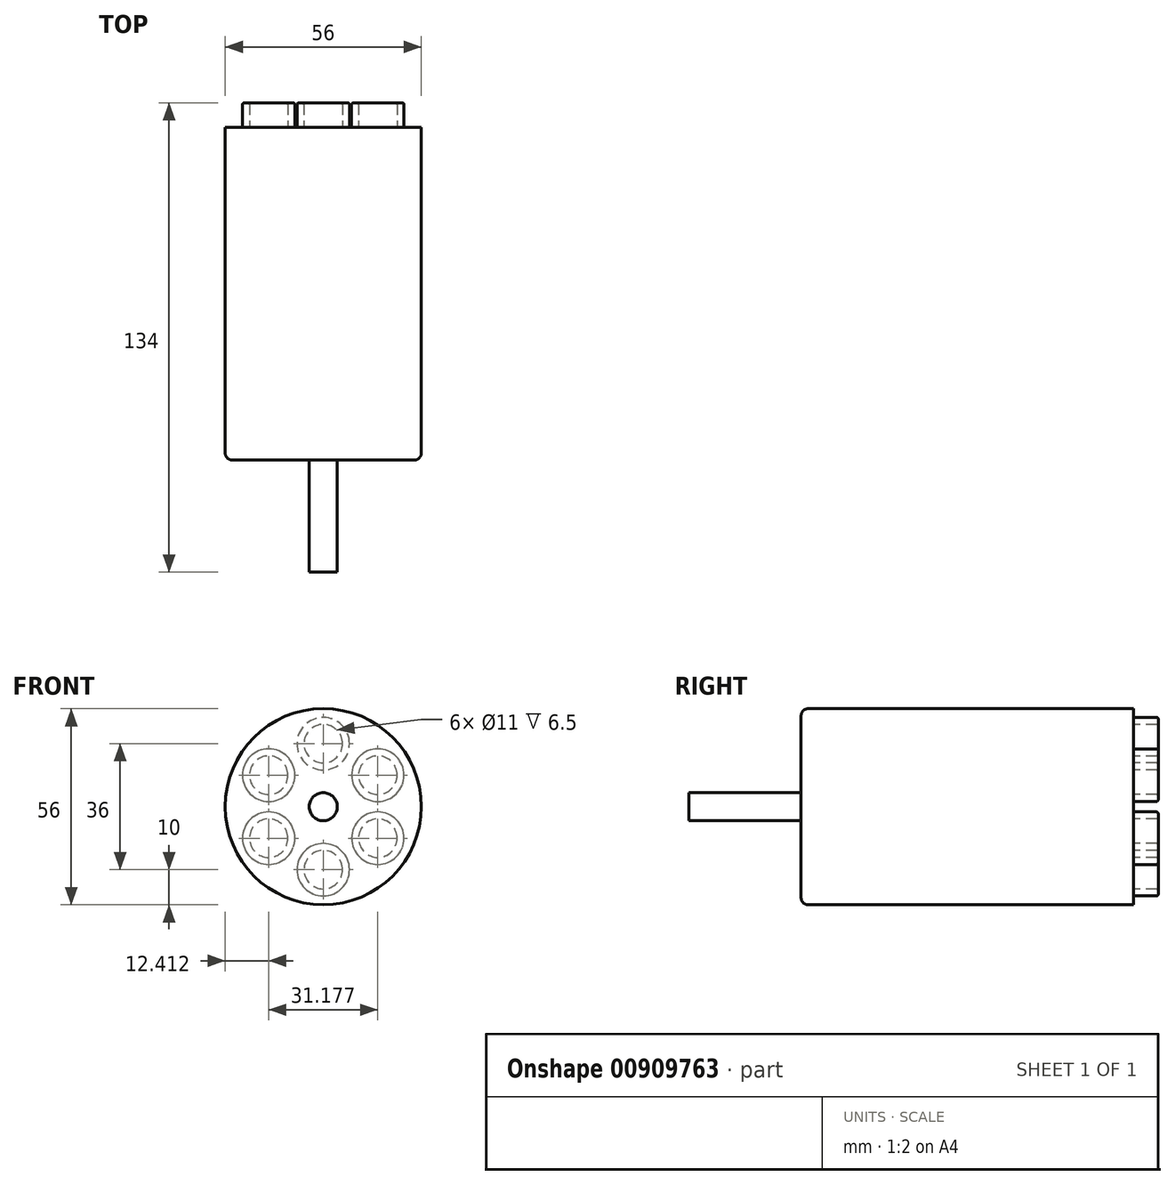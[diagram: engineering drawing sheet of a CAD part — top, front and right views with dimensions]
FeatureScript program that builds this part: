
annotation { "Feature Type Name" : "Feature", "Feature Type Description" : "" }
export const myFeature = defineFeature(function(context is Context, id is Id, definition is map)
    precondition{}
    {
        {
            var Q0;
            Q0=qCreatedBy(makeId("Front.planeOp"),FACE);
            var sketch = newSketch(context, id + "F0", { "sketchPlane" : qUnion([Q0])});
            skCircle(sketch, "E0", {"center": v(0, 0) * mm, "radius": 28 * mm});
            skSolve(sketch);
        }
        {
            var Q0;
            Q0 = qSketchRegion(id + "F0", true);
            extrude(context, id + "F1", {"entities" : qUnion([Q0]), "depth" : 95 * mm, "offsetDistance" : 25 * mm});
        }
        {
            var Q0;
            Q0=makeQuery(id+"F1.opExtrude","CAP_FACE",FACE,{"disambiguationData":[OSD([sQuery(id+"F0.wireOp",EDGE,"E0")])],"isStart":false});
            var sketch = newSketch(context, id + "F2", { "sketchPlane" : qUnion([Q0])});
            skCircle(sketch, "E1", {"center": v(0, 0) * mm, "radius": 4 * mm});
            skSolve(sketch);
        }
        {
            var Q0;
            Q0 = qSketchRegion(id + "F2", true);
            extrude(context, id + "F3", {"entities" : qUnion([Q0]), "operationType" : NewBodyOperationType.ADD, "depth" : 32 * mm, "offsetDistance" : 25 * mm});
        }
        {
            var Q0;
            Q0=makeQuery(id+"F1.opExtrude","CAP_FACE",FACE,{"disambiguationData":[OSD([sQuery(id+"F0.wireOp",EDGE,"E0")])],"isStart":true});
            var sketch = newSketch(context, id + "F4", { "sketchPlane" : qUnion([Q0])});
            skLineSegment(sketch, "E2", {"start": v(0, 0) * mm, "end": v(0, 18) * mm});
            skCircle(sketch, "E3", {"center": v(0, 18) * mm, "radius": 7.5 * mm});
            skCircle(sketch, "E4.1.0", {"center": v(-15.59, 9) * mm, "radius": 7.5 * mm});
            skLineSegment(sketch, "E4.1.1", {"start": v(0, 0) * mm, "end": v(-15.59, 9) * mm});
            skCircle(sketch, "E4.2.0", {"center": v(-15.59, -9) * mm, "radius": 7.5 * mm});
            skLineSegment(sketch, "E4.2.1", {"start": v(0, 0) * mm, "end": v(-15.59, -9) * mm});
            skCircle(sketch, "E4.3.0", {"center": v(0, -18) * mm, "radius": 7.5 * mm});
            skLineSegment(sketch, "E4.3.1", {"start": v(0, 0) * mm, "end": v(0, -18) * mm});
            skCircle(sketch, "E4.4.0", {"center": v(15.59, -9) * mm, "radius": 7.5 * mm});
            skLineSegment(sketch, "E4.4.1", {"start": v(0, 0) * mm, "end": v(15.59, -9) * mm});
            skCircle(sketch, "E4.5.0", {"center": v(15.59, 9) * mm, "radius": 7.5 * mm});
            skLineSegment(sketch, "E4.5.1", {"start": v(0, 0) * mm, "end": v(15.59, 9) * mm});
            skPoint(sketch, "E4.center", {"position": v(0, 0) * mm});
            skCircle(sketch, "E5", {"center": v(0, 18) * mm, "radius": 5.5 * mm});
            skCircle(sketch, "E6.1.0", {"center": v(-15.59, 9) * mm, "radius": 5.5 * mm});
            skCircle(sketch, "E6.2.0", {"center": v(-15.59, -9) * mm, "radius": 5.5 * mm});
            skCircle(sketch, "E6.3.0", {"center": v(0, -18) * mm, "radius": 5.5 * mm});
            skCircle(sketch, "E6.4.0", {"center": v(15.59, -9) * mm, "radius": 5.5 * mm});
            skCircle(sketch, "E6.5.0", {"center": v(15.59, 9) * mm, "radius": 5.5 * mm});
            skSolve(sketch);
        }
        {
            var Q0;
            Q0 = qSketchRegion(id + "F4", true);
            extrude(context, id + "F5", {"entities" : qUnion([Q0]), "operationType" : NewBodyOperationType.ADD, "depth" : 7 * mm, "offsetDistance" : 25 * mm});
        }
        {
            var Q0;
            Q0=makeQuery(id+"F5.opExtrude","CAP_EDGE",EDGE,{"disambiguationData":[OSD([sQuery(id+"F4.wireOp",EDGE,"E4.4.0")])],"isStart":false});
            var Q1;
            Q1=makeQuery(id+"F5.opExtrude","CAP_EDGE",EDGE,{"disambiguationData":[OSD([sQuery(id+"F4.wireOp",EDGE,"E6.4.0")])],"isStart":false});
            var Q2;
            Q2=makeQuery(id+"F5.opExtrude","CAP_EDGE",EDGE,{"disambiguationData":[OSD([sQuery(id+"F4.wireOp",EDGE,"E6.5.0")])],"isStart":false});
            var Q3;
            Q3=makeQuery(id+"F5.opExtrude","CAP_EDGE",EDGE,{"disambiguationData":[OSD([sQuery(id+"F4.wireOp",EDGE,"E4.5.0")])],"isStart":false});
            var Q4;
            Q4=makeQuery(id+"F5.opExtrude","CAP_EDGE",EDGE,{"disambiguationData":[OSD([sQuery(id+"F4.wireOp",EDGE,"E4.3.0")])],"isStart":false});
            var Q5;
            Q5=makeQuery(id+"F5.opExtrude","CAP_EDGE",EDGE,{"disambiguationData":[OSD([sQuery(id+"F4.wireOp",EDGE,"E6.3.0")])],"isStart":false});
            var Q6;
            Q6=makeQuery(id+"F5.opExtrude","CAP_EDGE",EDGE,{"disambiguationData":[OSD([sQuery(id+"F4.wireOp",EDGE,"E4.2.0")])],"isStart":false});
            var Q7;
            Q7=makeQuery(id+"F5.opExtrude","CAP_EDGE",EDGE,{"disambiguationData":[OSD([sQuery(id+"F4.wireOp",EDGE,"E6.2.0")])],"isStart":false});
            var Q8;
            Q8=makeQuery(id+"F5.opExtrude","CAP_EDGE",EDGE,{"disambiguationData":[OSD([sQuery(id+"F4.wireOp",EDGE,"E6.1.0")])],"isStart":false});
            var Q9;
            Q9=makeQuery(id+"F5.opExtrude","CAP_EDGE",EDGE,{"disambiguationData":[OSD([sQuery(id+"F4.wireOp",EDGE,"E4.1.0")])],"isStart":false});
            var Q10;
            Q10=makeQuery(id+"F5.opExtrude","CAP_EDGE",EDGE,{"disambiguationData":[OSD([sQuery(id+"F4.wireOp",EDGE,"E3")])],"isStart":false});
            var Q11;
            Q11=makeQuery(id+"F5.opExtrude","CAP_EDGE",EDGE,{"disambiguationData":[OSD([sQuery(id+"F4.wireOp",EDGE,"E5")])],"isStart":false});
            fillet(context, id + "F6", {"entities" : qUnion([Q0, Q1, Q2, Q3, Q4, Q5, Q6, Q7, Q8, Q9, Q10, Q11]), "radius" : .5 * mm, "tangentPropagation" : true, "allowEdgeOverflow" : false});
        }
        {
            var Q0;
            Q0=makeQuery(id+"F1.opExtrude","CAP_EDGE",EDGE,{"disambiguationData":[OSD([sQuery(id+"F0.wireOp",EDGE,"E0")])],"isStart":false});
            fillet(context, id + "F7", {"entities" : qUnion([Q0]), "radius" : 2 * mm, "tangentPropagation" : true, "allowEdgeOverflow" : false});
        }
    });
